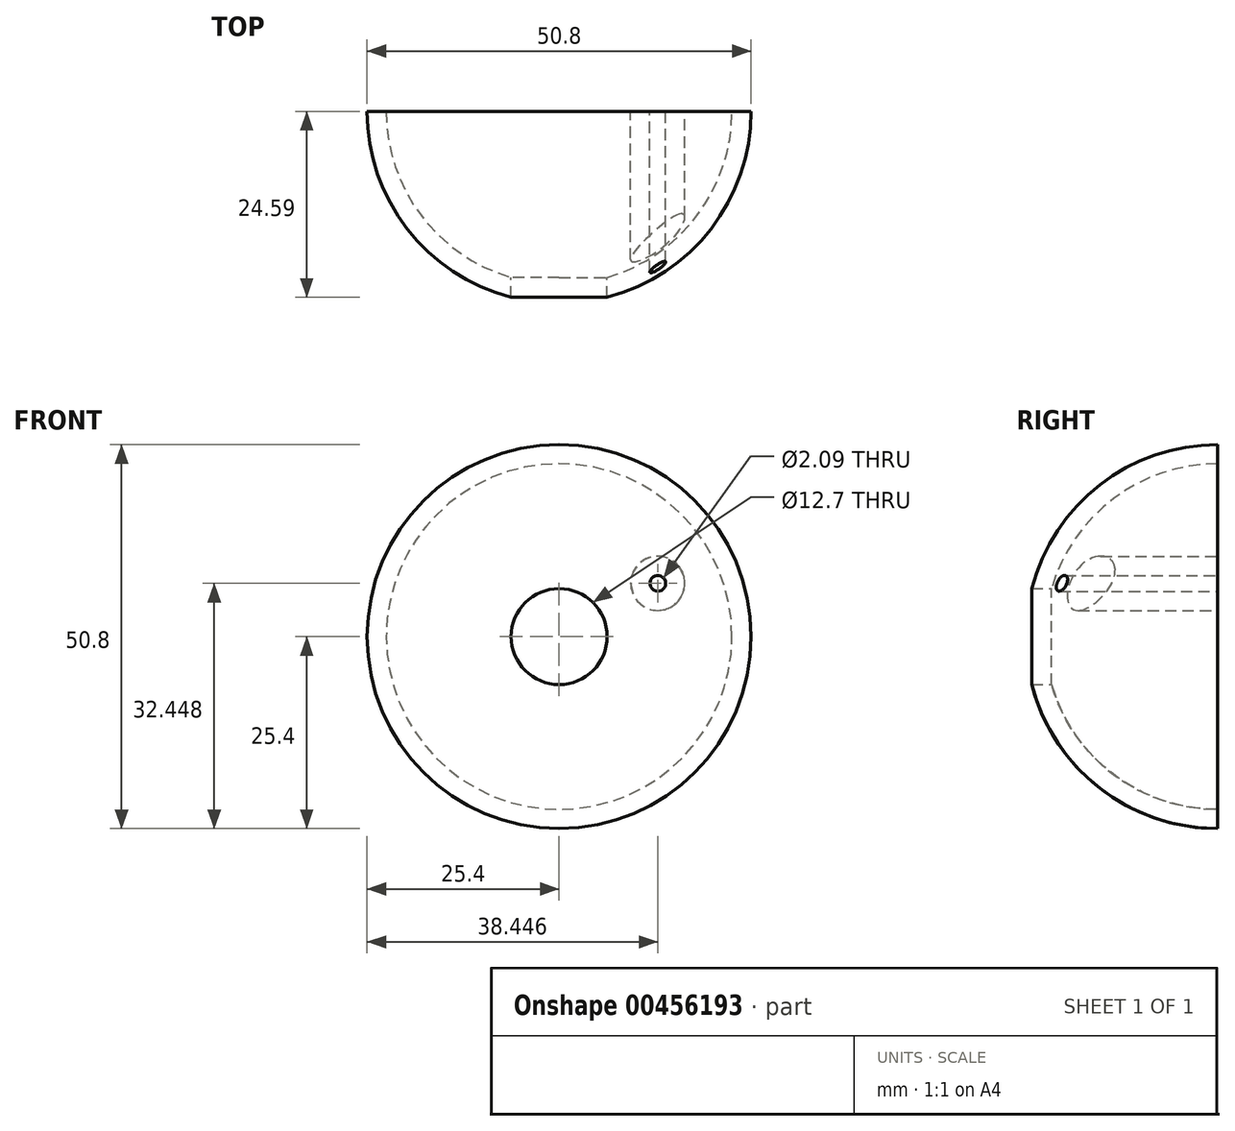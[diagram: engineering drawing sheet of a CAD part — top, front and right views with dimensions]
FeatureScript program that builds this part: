
annotation { "Feature Type Name" : "Feature", "Feature Type Description" : "" }
export const myFeature = defineFeature(function(context is Context, id is Id, definition is map)
    precondition{}
    {
        {
            var Q0;
            Q0=qCreatedBy(makeId("Front.planeOp"),FACE);
            var sketch = newSketch(context, id + "F0", { "sketchPlane" : qUnion([Q0])});
            skCircle(sketch, "E0", {"center": v(0, 0) * mm, "radius": 25.4 * mm});
            skCircle(sketch, "E1", {"center": v(13.05, 7.05) * mm, "radius": 1.04 * mm});
            skSolve(sketch);
        }
        {
            var Q0;
            Q0 = qSketchRegion(id + "F0", true);
            extrude(context, id + "F1", {"entities" : qUnion([Q0]), "depth" : 25.4 * mm});
        }
        {
            var Q0;
            Q0=makeQuery(id+"F1.opExtrude","CAP_EDGE",EDGE,{"disambiguationData":[OSD([sQuery(id+"F0.wireOp",EDGE,"E0")])],"isStart":false});
            fillet(context, id + "F2", {"entities" : qUnion([Q0]), "radius" : 25.4 * mm, "tangentPropagation" : true, "allowEdgeOverflow" : false});
        }
        {
            var Q0;
            Q0=makeQuery(id+"F1.opExtrude","CAP_FACE",FACE,{"disambiguationData":[OSD([sQuery(id+"F0.wireOp",EDGE,"E0"),sQuery(id+"F0.wireOp",EDGE,"E1")])],"isStart":true});
            shell(context, id + "F3", {"entities" : qUnion([Q0]), "thickness" : 2.54 * mm});
        }
        {
            var Q0;
            Q0=qCreatedBy(makeId("Front.planeOp"),FACE);
            var sketch = newSketch(context, id + "F4", { "sketchPlane" : qUnion([Q0])});
            skCircle(sketch, "E2", {"center": v(0, 0) * mm, "radius": 6.35 * mm});
            skSolve(sketch);
        }
        {
            var Q0;
            Q0 = qSketchRegion(id + "F4", true);
            extrude(context, id + "F5", {"entities" : qUnion([Q0]), "operationType" : NewBodyOperationType.REMOVE, "depth" : 50.8 * mm});
        }
    });
